# Revit family: НЕВАТОМ_Bходной конфузор VO в сейсмостойком исполнении, Версия 1
name_source: partatom
category: Оборудование
revit_build: Autodesk Revit 2017 (Build: 20170118_1100(x64)
units: mm (PartAtom-declared; Revit-internal decimal feet)

## family parameters
Всегда вертикально = Да
На основе рабочей плоскости = Нет
Общий = Нет
При загрузке вырезать с полостями = Нет
Размер круглого соединителя = Использовать диаметр
Тип детали = Нормальный
Точка расчета площади = Нет

## types (11) — shared parameters
ADSK_Завод-изготовитель = НЕВАТОМ
ADSK_Количество = 1

## per-type parameters (varying)
| type | ADSK_Масса | D | D1 | Dnf | Dnv | L | Nevatom_URL | R1 | R2 | R3 | R4 |
| Входной конфузор VO №4 | 6.6 | 400 мм | 500 мм | 550 мм | 480 мм | 88 мм |  | 275 мм | 250 мм | 200 мм | 240 мм |
| Входной конфузор VO №4,5 | 9 | 450 мм | 560 мм | 610 мм | 530 мм | 97 мм |  | 305 мм | 280 мм | 225 мм | 265 мм |
| Входной конфузор VO №5 | 11.6 | 500 мм | 630 мм | 680 мм | 590 мм | 115 мм |  | 340 мм | 315 мм | 250 мм | 295 мм |
| Входной конфузор VO №5,6 | 15.6 | 560 мм | 710 мм | 790 мм | 650 мм | 132 мм |  | 395 мм | 355 мм | 280 мм | 325 мм |
| Входной конфузор VO №6,3 | 19 | 630 мм | 800 мм | 864 мм | 730 мм | 150 мм |  | 432 мм | 400 мм | 315 мм | 365 мм |
| Входной конфузор VO №7,1 | 28.1 | 710 мм | 900 мм | 964 мм | 810 мм | 168 мм |  | 482 мм | 450 мм | 355 мм | 405 мм |
| Входной конфузор VO №8,0 | 33.6 | 800 мм | 1000 мм | 1080 мм | 900 мм | 176 мм |  | 540 мм | 500 мм | 400 мм | 450 мм |
| Входной конфузор VO №9,0 | 40 | 900 мм | 1120 мм | 1184 мм | 1010 мм | 193 мм | https://t.me | 592 мм | 560 мм | 450 мм | 505 мм |
| Входной конфузор VO №10,0 | 49 | 1000 мм | 1250 мм | 1330 мм | 1100 мм | 219 мм |  | 665 мм | 625 мм | 500 мм | 550 мм |
| Входной конфузор VO №11,2 | 65 | 1120 мм | 1400 мм | 1480 мм | 1230 мм | 245 мм |  | 740 мм | 700 мм | 560 мм | 615 мм |
| Входной конфузор VO №12,5 | 86 | 1250 мм | 1600 мм | 1680 мм | 1360 мм | 306 мм |  | 840 мм | 800 мм | 625 мм | 680 мм |
